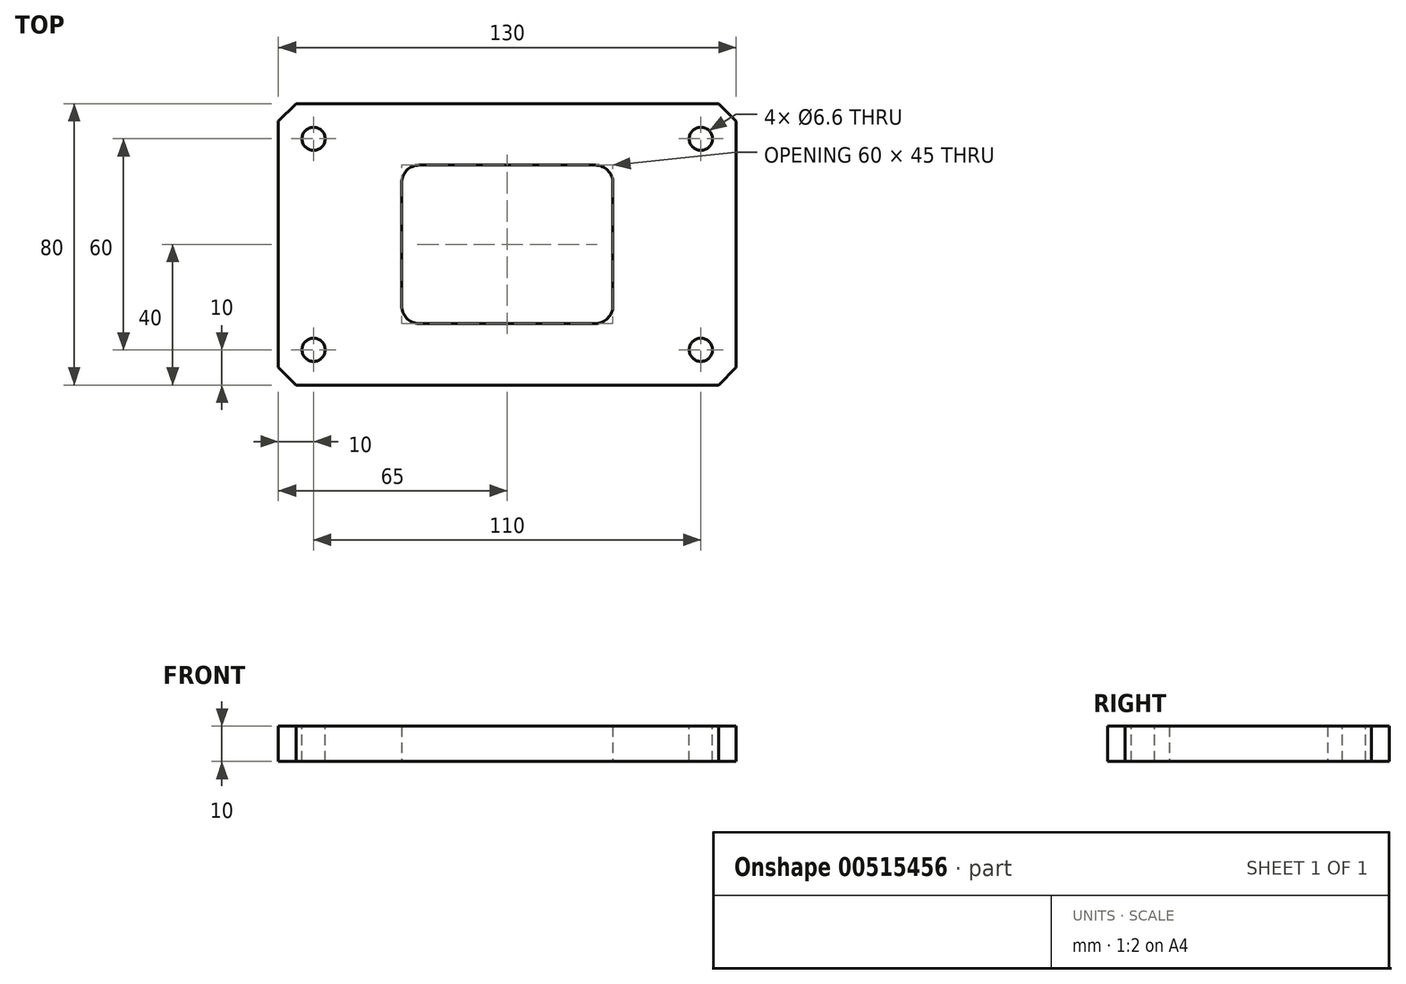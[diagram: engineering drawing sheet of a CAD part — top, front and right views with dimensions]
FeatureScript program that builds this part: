
annotation { "Feature Type Name" : "Feature", "Feature Type Description" : "" }
export const myFeature = defineFeature(function(context is Context, id is Id, definition is map)
    precondition{}
    {
        {
            var Q0;
            Q0=qCreatedBy(makeId("Top.planeOp"),FACE);
            var sketch = newSketch(context, id + "F0", { "sketchPlane" : qUnion([Q0])});
            skLineSegment(sketch, "E0.bottom", {"start": v(65, 40) * mm, "end": v(-65, 40) * mm});
            skLineSegment(sketch, "E0.top", {"start": v(65, -40) * mm, "end": v(-65, -40) * mm});
            skLineSegment(sketch, "E0.left", {"start": v(65, 40) * mm, "end": v(65, -40) * mm});
            skLineSegment(sketch, "E0.right", {"start": v(-65, 40) * mm, "end": v(-65, -40) * mm});
            skPoint(sketch, "E0.middle", {"position": v(0, 0) * mm});
            skLineSegment(sketch, "E1.bottom", {"start": v(30, 22.5) * mm, "end": v(-30, 22.5) * mm});
            skLineSegment(sketch, "E1.top", {"start": v(30, -22.5) * mm, "end": v(-30, -22.5) * mm});
            skLineSegment(sketch, "E1.left", {"start": v(30, 22.5) * mm, "end": v(30, -22.5) * mm});
            skLineSegment(sketch, "E1.right", {"start": v(-30, 22.5) * mm, "end": v(-30, -22.5) * mm});
            skSolve(sketch);
        }
        {
            var Q0;
            Q0=makeQuery(id+"F0.imprint","IMPRINT",FACE,{"disambiguationData":[TD([[makeQuery(id+"F0.imprint","IMPRINT",EDGE,{"derivedFrom":sQuery(id+"F0.wireOp",EDGE,"E0.bottom")}),1.0]])]});
            extrude(context, id + "F1", {"entities" : qUnion([Q0]), "depth" : 10 * mm, "offsetDistance" : 25 * mm});
        }
        {
            var Q0;
            Q0=makeQuery(id+"F1.opExtrude","CAP_FACE",FACE,{"disambiguationData":[OSD([sQuery(id+"F0.wireOp",EDGE,"E0.bottom"),sQuery(id+"F0.wireOp",EDGE,"E0.top"),sQuery(id+"F0.wireOp",EDGE,"E0.left"),sQuery(id+"F0.wireOp",EDGE,"E0.right"),sQuery(id+"F0.wireOp",EDGE,"E1.bottom"),sQuery(id+"F0.wireOp",EDGE,"E1.top"),sQuery(id+"F0.wireOp",EDGE,"E1.left"),sQuery(id+"F0.wireOp",EDGE,"E1.right")])],"isStart":false});
            var sketch = newSketch(context, id + "F2", { "sketchPlane" : qUnion([Q0])});
            skLineSegment(sketch, "E2.bottom", {"start": v(55, 30) * mm, "end": v(-55, 30) * mm, "construction": true});
            skLineSegment(sketch, "E2.top", {"start": v(55, -30) * mm, "end": v(-55, -30) * mm, "construction": true});
            skLineSegment(sketch, "E2.left", {"start": v(55, 30) * mm, "end": v(55, -30) * mm, "construction": true});
            skLineSegment(sketch, "E2.right", {"start": v(-55, 30) * mm, "end": v(-55, -30) * mm, "construction": true});
            skPoint(sketch, "E2.middle", {"position": v(0, 0) * mm});
            skSolve(sketch);
        }
        {
            var Q0;
            Q0=makeQuery(id+"F1.opExtrude","SWEPT_EDGE",EDGE,{"disambiguationData":[OSD([sQuery(id+"F0.wireOp",EDGE,"E1.bottom"),sQuery(id+"F0.wireOp",EDGE,"E1.right")])]});
            var Q1;
            Q1=makeQuery(id+"F1.opExtrude","SWEPT_EDGE",EDGE,{"disambiguationData":[OSD([sQuery(id+"F0.wireOp",EDGE,"E1.top"),sQuery(id+"F0.wireOp",EDGE,"E1.right")])]});
            var Q2;
            Q2=makeQuery(id+"F1.opExtrude","SWEPT_EDGE",EDGE,{"disambiguationData":[OSD([sQuery(id+"F0.wireOp",EDGE,"E1.top"),sQuery(id+"F0.wireOp",EDGE,"E1.left")])]});
            var Q3;
            Q3=makeQuery(id+"F1.opExtrude","SWEPT_EDGE",EDGE,{"disambiguationData":[OSD([sQuery(id+"F0.wireOp",EDGE,"E1.bottom"),sQuery(id+"F0.wireOp",EDGE,"E1.left")])]});
            fillet(context, id + "F3", {"entities" : qUnion([Q0, Q1, Q2, Q3]), "radius" : 5 * mm, "tangentPropagation" : true, "allowEdgeOverflow" : false});
        }
        {
            var Q0;
            Q0=makeQuery(id+"F1.opExtrude","SWEPT_EDGE",EDGE,{"disambiguationData":[OSD([sQuery(id+"F0.wireOp",EDGE,"E0.top"),sQuery(id+"F0.wireOp",EDGE,"E0.right")])]});
            var Q1;
            Q1=makeQuery(id+"F1.opExtrude","SWEPT_EDGE",EDGE,{"disambiguationData":[OSD([sQuery(id+"F0.wireOp",EDGE,"E0.bottom"),sQuery(id+"F0.wireOp",EDGE,"E0.right")])]});
            var Q2;
            Q2=makeQuery(id+"F1.opExtrude","SWEPT_EDGE",EDGE,{"disambiguationData":[OSD([sQuery(id+"F0.wireOp",EDGE,"E0.top"),sQuery(id+"F0.wireOp",EDGE,"E0.left")])]});
            var Q3;
            Q3=makeQuery(id+"F1.opExtrude","SWEPT_EDGE",EDGE,{"disambiguationData":[OSD([sQuery(id+"F0.wireOp",EDGE,"E0.bottom"),sQuery(id+"F0.wireOp",EDGE,"E0.left")])]});
            chamfer(context, id + "F4", {"entities" : qUnion([Q0, Q1, Q2, Q3]), "width" : 5 * mm, "tangentPropagation" : true});
        }
        {
            var Q0;
            Q0=sQuery(id+"F2.wireOp",VERTEX,"E2.right.start");
            var Q1;
            Q1=sQuery(id+"F2.wireOp",VERTEX,"E2.top.end");
            var Q2;
            Q2=sQuery(id+"F2.wireOp",VERTEX,"E2.left.end");
            var Q3;
            Q3=sQuery(id+"F2.wireOp",VERTEX,"E2.left.start");
            var Q4;
            Q4=makeQuery(id+"F1.opExtrude","SWEPT_BODY",BODY,{"disambiguationData":[OSD([sQuery(id+"F0.wireOp",EDGE,"E0.bottom"),sQuery(id+"F0.wireOp",EDGE,"E0.top"),sQuery(id+"F0.wireOp",EDGE,"E0.left"),sQuery(id+"F0.wireOp",EDGE,"E0.right"),sQuery(id+"F0.wireOp",EDGE,"E1.bottom"),sQuery(id+"F0.wireOp",EDGE,"E1.top"),sQuery(id+"F0.wireOp",EDGE,"E1.left"),sQuery(id+"F0.wireOp",EDGE,"E1.right")])]});
            hole(context, id + "F5", {"style" : HoleStyle.SIMPLE, "endStyle" : HoleEndStyle.BLIND, "standardTappedOrClearance" : lookupTablePath({ "standard" : "ISO", "fit" : "Normal", "size" : "M6", "type" : "Clearance" }), "standardBlindInLast" : lookupTablePath({ "fit" : "Standard", "standard" : "ISO", "size" : "M6", "type" : "Clearance" }), "holeDiameter" : 6.6 * mm, "holeDepth" : 20 * mm, "isTappedThrough" : true, "tappedDepth" : 12 * mm, "tapClearance" : 3, "locations" : qUnion([Q0, Q1, Q2, Q3]), "scope" : qUnion([Q4])});
        }
    });
